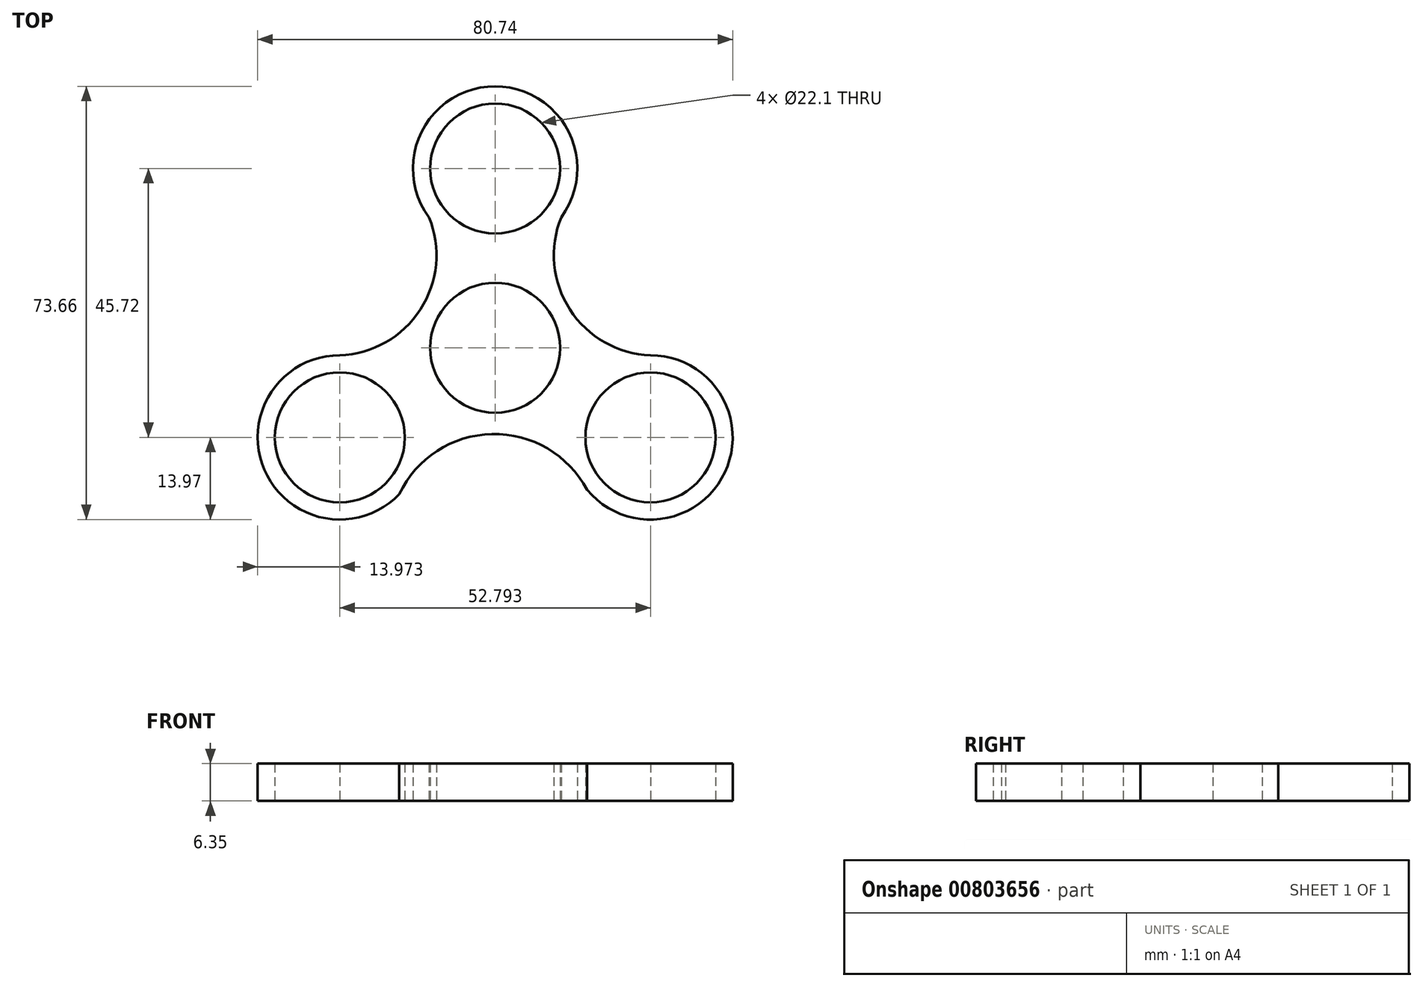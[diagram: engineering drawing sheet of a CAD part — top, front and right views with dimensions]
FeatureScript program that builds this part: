
annotation { "Feature Type Name" : "Feature", "Feature Type Description" : "" }
export const myFeature = defineFeature(function(context is Context, id is Id, definition is map)
    precondition{}
    {
        {
            var Q0;
            Q0=qCreatedBy(makeId("Top.planeOp"),FACE);
            var sketch = newSketch(context, id + "F0", { "sketchPlane" : qUnion([Q0])});
            skCircle(sketch, "E0", {"center": v(0, 0) * mm, "radius": 44.45 * mm});
            skCircle(sketch, "E1", {"center": v(0, 0) * mm, "radius": 11.05 * mm});
            skLineSegment(sketch, "E2", {"start": v(0, 0) * mm, "end": v(0, 30.48) * mm});
            skCircle(sketch, "E3", {"center": v(0, 30.48) * mm, "radius": 11.05 * mm});
            skCircle(sketch, "E4.1.0", {"center": v(-26.4, -15.24) * mm, "radius": 11.05 * mm});
            skCircle(sketch, "E4.2.0", {"center": v(26.4, -15.24) * mm, "radius": 11.05 * mm});
            skSolve(sketch);
        }
        {
            var Q0;
            Q0=makeQuery(id+"F0.imprint","IMPRINT",FACE,{"disambiguationData":[TD([[makeQuery(id+"F0.imprint","IMPRINT",EDGE,{"derivedFrom":sQuery(id+"F0.wireOp",EDGE,"E0")}),1.0]])]});
            var sketch = newSketch(context, id + "F1", { "sketchPlane" : qUnion([Q0])});
            skCircle(sketch, "E5", {"center": v(0, 0) * mm, "radius": 13.97 * mm});
            skLineSegment(sketch, "E6", {"start": v(0, 0) * mm, "end": v(0, 30.48) * mm});
            skCircle(sketch, "E7", {"center": v(0, 30.48) * mm, "radius": 13.97 * mm});
            skCircle(sketch, "E8.1.0", {"center": v(-26.4, -15.24) * mm, "radius": 13.97 * mm});
            skCircle(sketch, "E8.2.0", {"center": v(26.4, -15.24) * mm, "radius": 13.97 * mm});
            skArc(sketch, "E9", {"start": v(-26.4, -1.27) * mm, "mid": v(-12.7, 6.5) * mm, "end": v(-11.23, 22.18) * mm});
            skArc(sketch, "E10", {"start": v(11.23, 22.18) * mm, "mid": v(12.72, 6.5) * mm, "end": v(26.4, -1.27) * mm});
            skArc(sketch, "E11", {"start": v(15.65, -24.16) * mm, "mid": v(-0.54, -14.68) * mm, "end": v(-16.29, -24.88) * mm});
            skSolve(sketch);
        }
        {
            var Q0;
            Q0=makeQuery(id+"F1.imprint","IMPRINT",FACE,{"disambiguationData":[TD([[makeQuery(id+"F1.imprint","IMPRINT",EDGE,{"derivedFrom":makeQuery(id+"F0.imprint","IMPRINT",EDGE,{"derivedFrom":sQuery(id+"F0.wireOp",EDGE,"E3")})}),-1.0]])]});
            var Q1;
            Q1=makeQuery(id+"F1.imprint","IMPRINT",FACE,{"disambiguationData":[TD([[makeQuery(id+"F1.imprint","IMPRINT",EDGE,{"derivedFrom":makeQuery(id+"F0.imprint","IMPRINT",EDGE,{"derivedFrom":sQuery(id+"F0.wireOp",EDGE,"E4.2.0")})}),-1.0]])]});
            var Q2;
            Q2=makeQuery(id+"F1.imprint","IMPRINT",FACE,{"disambiguationData":[TD([[makeQuery(id+"F1.imprint","IMPRINT",EDGE,{"derivedFrom":makeQuery(id+"F0.imprint","IMPRINT",EDGE,{"derivedFrom":sQuery(id+"F0.wireOp",EDGE,"E4.1.0")})}),-1.0]])]});
            var Q3;
            Q3=makeQuery(id+"F1.imprint","IMPRINT",FACE,{"disambiguationData":[TD([[makeQuery(id+"F1.imprint","IMPRINT",EDGE,{"derivedFrom":sQuery(id+"F1.wireOp",EDGE,"E5")}),-1.0]])]});
            extrude(context, id + "F2", {"entities" : qUnion([Q0, Q1, Q2, Q3]), "depth" : 6.35 * mm, "offsetDistance" : 25.4 * mm});
        }
        {
            var Q0;
            Q0=makeQuery(id+"F0.imprint","IMPRINT",FACE,{"disambiguationData":[TD([[makeQuery(id+"F0.imprint","IMPRINT",EDGE,{"derivedFrom":sQuery(id+"F0.wireOp",EDGE,"E0")}),1.0]])]});
            var sketch = newSketch(context, id + "F3", { "sketchPlane" : qUnion([Q0])});
            skCircle(sketch, "E12", {"center": v(0, 0) * mm, "radius": 13.97 * mm});
            skSolve(sketch);
        }
        {
            var Q0;
            Q0=makeQuery(id+"F3.imprint","IMPRINT",FACE,{"disambiguationData":[TD([[makeQuery(id+"F3.imprint","IMPRINT",EDGE,{"derivedFrom":sQuery(id+"F3.wireOp",EDGE,"E12")}),1.0]])]});
            extrude(context, id + "F4", {"entities" : qUnion([Q0]), "operationType" : NewBodyOperationType.ADD, "depth" : 6.35 * mm, "offsetDistance" : 25.4 * mm});
        }
        {
            var Q0;
            Q0=makeQuery(id+"F0.imprint","IMPRINT",FACE,{"disambiguationData":[TD([[makeQuery(id+"F0.imprint","IMPRINT",EDGE,{"derivedFrom":sQuery(id+"F0.wireOp",EDGE,"E0")}),1.0]])]});
            extrude(context, id + "F5", {"entities" : qUnion([Q0]), "operationType" : NewBodyOperationType.REMOVE, "endBound" : BoundingType.THROUGH_ALL, "oppositeDirection" : true, "depth" : 25.4 * mm, "offsetDistance" : 25.4 * mm});
        }
        {
            var Q0;
            Q0=makeQuery(id+"F4.boolean.opBoolean","MERGE",FACE,{"derivedFrom":[makeQuery(id+"F2.opExtrude","CAP_FACE",FACE,{"disambiguationData":[OSD([sQuery(id+"F0.wireOp",EDGE,"E3"),sQuery(id+"F0.wireOp",EDGE,"E4.1.0"),sQuery(id+"F0.wireOp",EDGE,"E4.2.0"),sQuery(id+"F1.wireOp",EDGE,"E5"),sQuery(id+"F1.wireOp",EDGE,"E7"),sQuery(id+"F1.wireOp",EDGE,"E8.1.0"),sQuery(id+"F1.wireOp",EDGE,"E8.2.0"),sQuery(id+"F1.wireOp",EDGE,"E9"),sQuery(id+"F1.wireOp",EDGE,"E10"),sQuery(id+"F1.wireOp",EDGE,"E11")])],"isStart":false}),makeQuery(id+"F4.opExtrude","CAP_FACE",FACE,{"disambiguationData":[OSD([sQuery(id+"F0.wireOp",EDGE,"E1"),sQuery(id+"F3.wireOp",EDGE,"E12")])],"isStart":false})]});
            var sketch = newSketch(context, id + "F6", { "sketchPlane" : qUnion([Q0])});
            skLineSegment(sketch, "E13", {"start": v(-26.4, -1.27) * mm, "end": v(-26.4, 15.76) * mm});
            skLineSegment(sketch, "E14", {"start": v(-11.23, 22.18) * mm, "end": v(-26.4, 15.76) * mm});
            skLineSegment(sketch, "E15", {"start": v(-13.38, 26.45) * mm, "end": v(-26.4, 20.94) * mm});
            skLineSegment(sketch, "E16", {"start": v(-26.4, -1.27) * mm, "end": v(-31.49, -2.23) * mm});
            skLineSegment(sketch, "E17", {"start": v(-26.4, 20.94) * mm, "end": v(-31.49, 18.79) * mm});
            skLineSegment(sketch, "E18", {"start": v(-31.49, -2.23) * mm, "end": v(-31.49, 18.79) * mm});
            skSolve(sketch);
        }
        {
            var Q0;
            Q0=makeQuery(id+"F6.imprint","IMPRINT",FACE,{"disambiguationData":[TD([[makeQuery(id+"F6.imprint","IMPRINT",EDGE,{"derivedFrom":sQuery(id+"F6.wireOp",EDGE,"E13")}),-1.0]])]});
            extrude(context, id + "F7", {"entities" : qUnion([Q0]), "operationType" : NewBodyOperationType.REMOVE, "endBound" : BoundingType.THROUGH_ALL, "oppositeDirection" : true, "depth" : 25.4 * mm, "offsetDistance" : 25.4 * mm});
        }
    });
